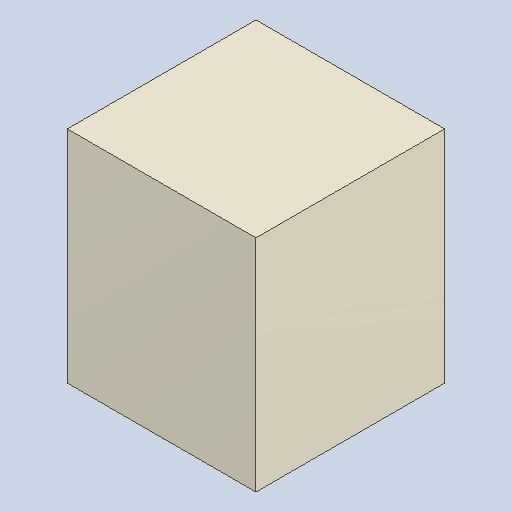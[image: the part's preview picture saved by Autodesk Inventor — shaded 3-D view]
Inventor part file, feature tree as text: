
AUTODESK INVENTOR PART (.ipt)
format: ipt  version: 2023.4 (Build 274418000, 418)  size: 82,944 bytes
history: native  units: mm
features: extrude x1
ambient origin geometry x8: Origin, YZ Plane, XZ Plane, XY Plane, X Axis, Y Axis, Z Axis, Center Point
bodies: Solid1 (feature_tree)
feature tree (1):
  extrude  "Extruded_27"  [1 undecoded]
note: 1 required parameter value undecoded (feature->parameter linkage not recoverable at this tier; creation-order binding heuristic only, values carry confidence <= 0.55)
